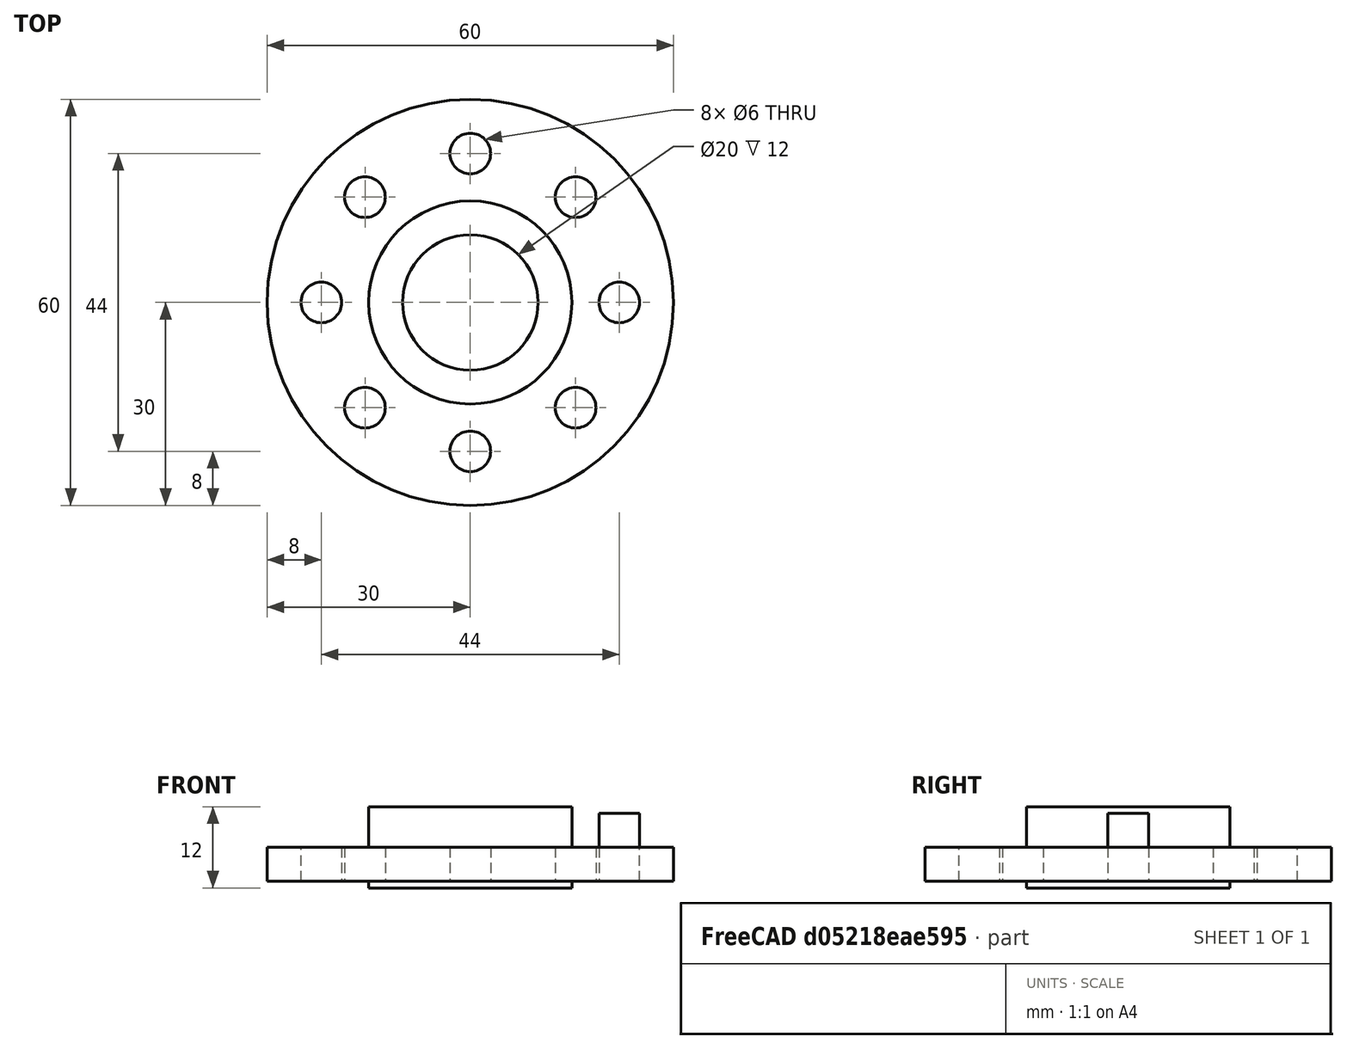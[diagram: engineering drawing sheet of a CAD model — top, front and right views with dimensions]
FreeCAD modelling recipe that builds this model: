
FCSTD DOCUMENT  (FreeCAD 0.21R33694 (Git))
Label: OJT1_T11P02_brida
License: All rights reserved
LicenseURL: http://en.wikipedia.org/wiki/All_rights_reserved
objects: Part::Cylinder×4, Part::Cut×2, Part::MultiFuse×1, Part::FeaturePython×1
note: 7 computed .brp shape members not serialized (recipe doc carries the construction recipe); baked Part::Feature solids carry a one-line shape summary decoded from their .brp

FEATURE [Part::Cylinder] Cylinder  label="Base"
  Angle = 360
  AttacherType = Attacher::AttachEngine3D
  FirstAngle = 0
  Height = 5
  Radius = 30
  SecondAngle = 0
FEATURE [Part::Cylinder] Cylinder001  label="tubo_exterior"
  Angle = 360
  AttacherType = Attacher::AttachEngine3D
  FirstAngle = 0
  Height = 12
  Placement = pos=(0,0,-1) rot=(0,0,1;0rad)
  Radius = 15
  SecondAngle = 0
FEATURE [Part::Cylinder] Cylinder002  label="tubo_interior"
  Angle = 360
  AttacherType = Attacher::AttachEngine3D
  FirstAngle = 0
  Height = 30
  Placement = pos=(0,0,-1) rot=(0,0,1;0rad)
  Radius = 10
  SecondAngle = 0
FEATURE [Part::MultiFuse] Fusion
  Refine = true
  Shapes = -> [Cylinder,Cylinder001]
FEATURE [Part::Cut] Cut
  Base = -> Fusion
  Refine = true
  Tool = -> Cylinder002
FEATURE [Part::Cylinder] Cylinder003  label="Cylinder"
  Angle = 360
  AttacherType = Attacher::AttachEngine3D
  FirstAngle = 0
  Height = 10
  Placement = pos=(22,0,0) rot=(0,0,1;0rad)
  Radius = 3
  SecondAngle = 0
FEATURE [Part::FeaturePython] Array  # Draft array (typed FeaturePython)
  AlwaysSyncPlacement = false
  Angle = 360
  ArrayType = 1
  Axis = (0,0,1)
  Base = -> Cylinder003
  Center = (0,0,0)
  Count = 8
  ExpandArray = false
  Fuse = false
  IntervalAxis = (0,0,0)
  IntervalX = (50,0,0)
  IntervalY = (0,50,0)
  IntervalZ = (0,0,50)
  NumberCircles = 3
  NumberPolar = 8
  NumberX = 2
  NumberY = 2
  NumberZ = 1
  Placement = pos=(0,0,-1) rot=(0,0,1;0rad)
  PlacementList = 8 placements: [(22,0,0),(15.5563,15.5563,0),(0,22,0),(-15.5563,15.5563,0),(-22,2.69422e-15,0),(-15.5563,-15.5563,0),(-4.88498e-15,-22,0),(15.5563,-15.5563,0)]
  RadialDistance = 50
  ScaleList = (8) [(1,1,1),(1,1,1),(1,1,1),(1,1,1),(1,1,1),(1,1,1),(1,1,1),(1,1,1)]
  Symmetry = 1
  TangentialDistance = 25
FEATURE [Part::Cut] Cut001
  Base = -> Cut
  Refine = true
  Tool = -> Array
